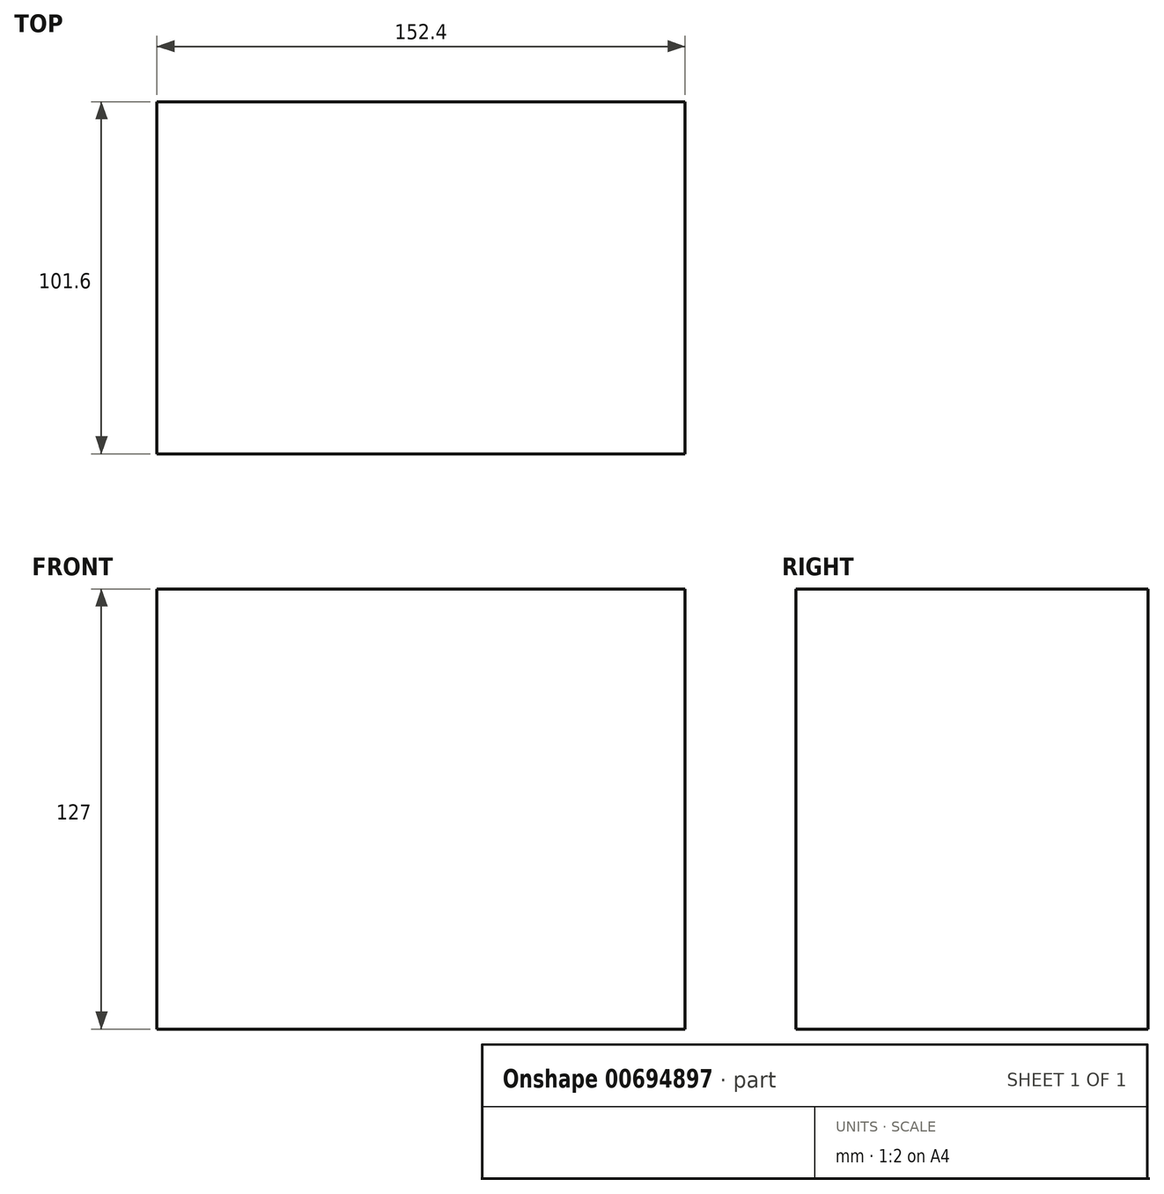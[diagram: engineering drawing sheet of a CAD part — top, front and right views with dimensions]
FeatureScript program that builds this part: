
annotation { "Feature Type Name" : "Feature", "Feature Type Description" : "" }
export const myFeature = defineFeature(function(context is Context, id is Id, definition is map)
    precondition{}
    {
        {
            var Q0;
            Q0=qCreatedBy(makeId("Front.planeOp"),FACE);
            var sketch = newSketch(context, id + "F0", { "sketchPlane" : qUnion([Q0])});
            skLineSegment(sketch, "E0.bottom", {"start": v(-108.9, 78.03) * mm, "end": v(43.5, 78.03) * mm});
            skLineSegment(sketch, "E0.top", {"start": v(-108.9, -48.97) * mm, "end": v(43.5, -48.97) * mm});
            skLineSegment(sketch, "E0.left", {"start": v(-108.9, 78.03) * mm, "end": v(-108.9, -48.97) * mm});
            skLineSegment(sketch, "E0.right", {"start": v(43.5, 78.03) * mm, "end": v(43.5, -48.97) * mm});
            skSolve(sketch);
        }
        {
            var Q0;
            Q0=makeQuery(id+"F0.imprint","IMPRINT",FACE,{"disambiguationData":[TD([[makeQuery(id+"F0.imprint","IMPRINT",EDGE,{"derivedFrom":sQuery(id+"F0.wireOp",EDGE,"E0.bottom")}),-1.0]])]});
            extrude(context, id + "F1", {"entities" : qUnion([Q0]), "depth" : 101.6 * mm, "offsetDistance" : 25.4 * mm});
        }
    });
